# Revit family: Building-IEC309Connections-GEWISS-COMBIBLOC_BOARD_2SOCKETS
name_source: partatom
category: Apparecchi elettrici
units: mm (PartAtom-declared; Revit-internal decimal feet)

## family parameters
Condiviso = No
Host = Superficie
Mantenere orientamento annotazione = Sì
Punto di calcolo locali = Sì
Quota connettore circolare = Usa diametro
Taglio con vuoti quando caricato = No
Tipo di parte = Normale

## types (1)
- GW66492 - BOARD IP55 EMPTY VERT. COMBIBLOC 2 SOCK
    Accessories supplied = 70 °C
    Accordance with Standards = EN 62208
    Catalogue = BUILDING
    Colour = Grey RAL 7035
    Descrizione = BOARD IP55 EMPTY VERT. COMBIBLOC 2 SOCK
    Dispersible power (W) = 13
    Electrocod = 0321
    For socket-outlets = Compact
    Glow Wire Test = 650°C
    Glow wire test: = Empty
    IDF = 87e27bb4-cea2-4223-b5d9-d33036627ed7
    IDT = eb3db09c38ad46b3b0133e3f89be51f6
    IP degree = IP55
    Installation type = Surface-mounting
    Insulation class = II
    Modello = GW66492
    No. IB socket-outlets houseable = 2 COMBIBLOC 16/32A
    No. of blank lids supplied = 1
    No. of modules EN 50022 = 8
    Operating temperature: = -25 +40 °C
    Produttore = GEWISS S.p.A.
    Prospetto di default = 1219 mm
    SEO = Board
    STRUTTURA = RAL - 7035
    STRUTTURA ALTA = Poche
    Shock resistance = IK08
    Spostamento_S = 1420 mm  [stored 4.65879 ft]
    Technical sheet = https://www.gewiss.com
    Thermo-pressure with ball = 70
    URL = https://www.gewiss.com
    Version file RFA = 21.10
    Version type = Empty

note: source unit labels omitted for Thermo-pressure with ball — the stored unit's dimension contradicts the parameter name (converter mislabeling)

note: [stored X ft] marks values corroborated as IEEE doubles in the binary element streams (Revit-internal decimal feet)

## geometry (parser evidence)
native form markers: Sweep x1
no freeform markers — native parametric forms only
